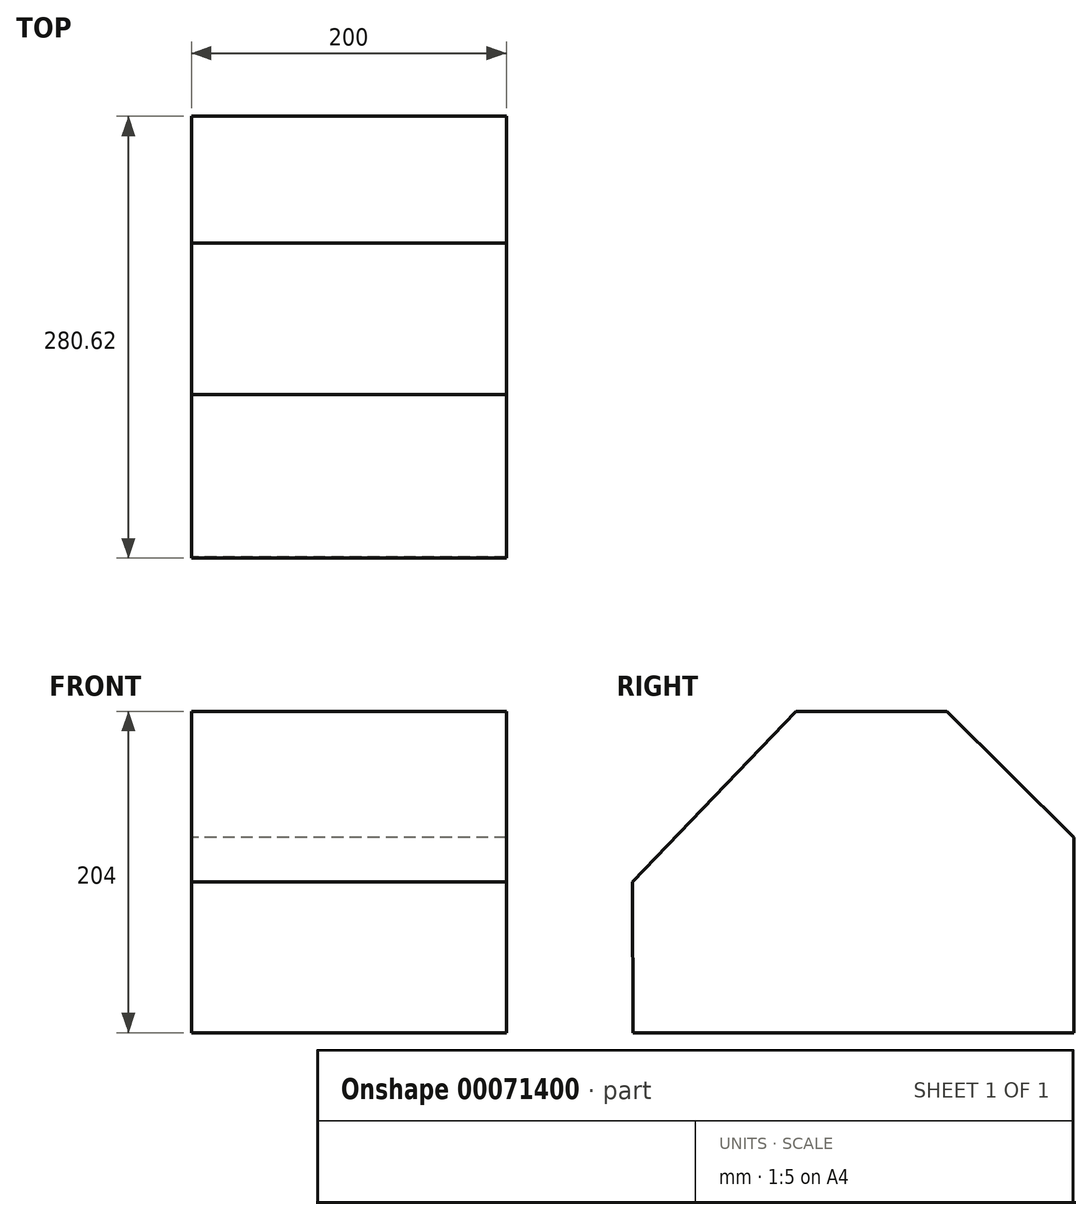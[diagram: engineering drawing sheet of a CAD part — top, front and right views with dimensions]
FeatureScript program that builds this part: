
annotation { "Feature Type Name" : "Feature", "Feature Type Description" : "" }
export const myFeature = defineFeature(function(context is Context, id is Id, definition is map)
    precondition{}
    {
        {
            var Q0;
            Q0=qCreatedBy(makeId("Right.planeOp"),FACE);
            var sketch = newSketch(context, id + "F0", { "sketchPlane" : qUnion([Q0])});
            skLineSegment(sketch, "E0", {"start": v(-145.7, 0) * mm, "end": v(-41.8, 108.2) * mm});
            skLineSegment(sketch, "E1", {"start": v(-41.8, 108.2) * mm, "end": v(54.3, 108.2) * mm});
            skLineSegment(sketch, "E2", {"start": v(54.3, 108.2) * mm, "end": v(134.92, 28.2) * mm});
            skLineSegment(sketch, "E3", {"start": v(134.92, 28.2) * mm, "end": v(134.92, -95.8) * mm});
            skLineSegment(sketch, "E4", {"start": v(134.92, -95.8) * mm, "end": v(-145.08, -95.8) * mm});
            skLineSegment(sketch, "E5", {"start": v(-145.08, -95.8) * mm, "end": v(-145.7, 0) * mm});
            skSolve(sketch);
        }
        {
            var Q0;
            Q0=makeQuery(id+"F0.imprint","IMPRINT",FACE,{"disambiguationData":[TD([[makeQuery(id+"F0.imprint","IMPRINT",EDGE,{"derivedFrom":sQuery(id+"F0.wireOp",EDGE,"E0")}),-1.0]])]});
            extrude(context, id + "F1", {"entities" : qUnion([Q0]), "depth" : 200 * mm});
        }
    });
